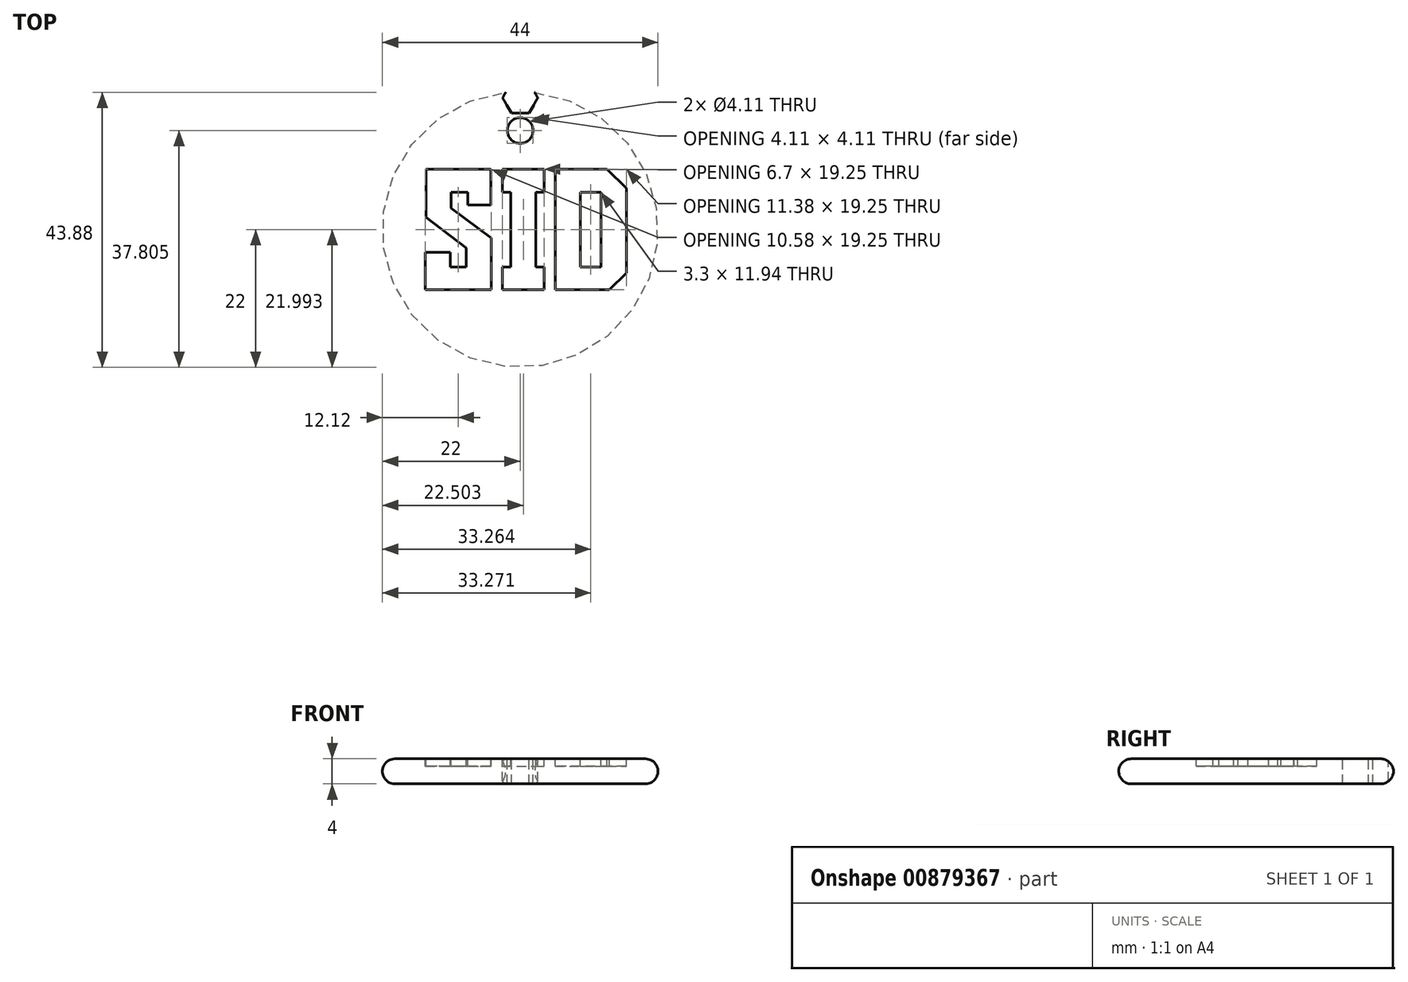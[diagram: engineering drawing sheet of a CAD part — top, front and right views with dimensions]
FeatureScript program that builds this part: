
annotation { "Feature Type Name" : "Feature", "Feature Type Description" : "" }
export const myFeature = defineFeature(function(context is Context, id is Id, definition is map)
    precondition{}
    {
        {
            var Q0;
            Q0=qCreatedBy(makeId("Front.planeOp"),FACE);
            var sketch = newSketch(context, id + "F0", { "sketchPlane" : qUnion([Q0])});
            skLineSegment(sketch, "E0.bottom", {"start": v(0, 0) * mm, "end": v(-20, 0) * mm});
            skLineSegment(sketch, "E0.top", {"start": v(0, 4) * mm, "end": v(-20, 4) * mm});
            skLineSegment(sketch, "E0.left", {"start": v(0, 0) * mm, "end": v(0, 4) * mm});
            skLineSegment(sketch, "E0.right", {"start": v(-20, 0) * mm, "end": v(-20, 4) * mm});
            skArc(sketch, "E1", {"start": v(-20, 4) * mm, "mid": v(-22, 2) * mm, "end": v(-20, 0) * mm});
            skSolve(sketch);
        }
        {
            var Q0;
            Q0=makeQuery(id+"F0.imprint","IMPRINT",FACE,{"disambiguationData":[TD([[makeQuery(id+"F0.imprint","IMPRINT",EDGE,{"derivedFrom":sQuery(id+"F0.wireOp",EDGE,"E0.right")}),1.0]])]});
            var Q1;
            Q1=makeQuery(id+"F0.imprint","IMPRINT",FACE,{"disambiguationData":[TD([[makeQuery(id+"F0.imprint","IMPRINT",EDGE,{"derivedFrom":sQuery(id+"F0.wireOp",EDGE,"E0.bottom")}),-1.0]])]});
            var Q2;
            Q2=sQuery(id+"F0.wireOp",EDGE,"E0.left");
            revolve(context, id + "F1", {"surfaceOperationType" : NewSurfaceOperationType.NEW, "entities" : qUnion([Q0, Q1]), "axis" : qUnion([Q2]), "revolveType" : RevolveType.FULL});
        }
        {
            var Q0;
            Q0=makeQuery(id+"F1.opRevolve","SWEPT_FACE",FACE,{"disambiguationData":[OSD([sQuery(id+"F0.wireOp",EDGE,"E0.top")])]});
            var sketch = newSketch(context, id + "F2", { "sketchPlane" : qUnion([Q0])});
            skLineSegment(sketch, "E2", {"start": v(-4.59, -9.62) * mm, "end": v(-15.17, -9.62) * mm});
            skLineSegment(sketch, "E3", {"start": v(-15.17, -9.62) * mm, "end": v(-15.17, -3.63) * mm});
            skLineSegment(sketch, "E4", {"start": v(-15.17, -3.63) * mm, "end": v(-11.14, -3.63) * mm});
            skLineSegment(sketch, "E5", {"start": v(-11.14, -3.63) * mm, "end": v(-11.14, -5.98) * mm});
            skLineSegment(sketch, "E6", {"start": v(-11.14, -5.98) * mm, "end": v(-8.64, -5.98) * mm});
            skLineSegment(sketch, "E7", {"start": v(-8.64, -5.98) * mm, "end": v(-8.64, -2.92) * mm});
            skLineSegment(sketch, "E8", {"start": v(-8.64, -2.92) * mm, "end": v(-15.04, 1.92) * mm});
            skLineSegment(sketch, "E9", {"start": v(-15.04, 1.92) * mm, "end": v(-15.04, 9.62) * mm});
            skLineSegment(sketch, "E10", {"start": v(-15.04, 9.62) * mm, "end": v(-4.7, 9.62) * mm});
            skLineSegment(sketch, "E11", {"start": v(-4.7, 9.62) * mm, "end": v(-4.7, 3.9) * mm});
            skLineSegment(sketch, "E12", {"start": v(-4.7, 3.9) * mm, "end": v(-8.37, 3.9) * mm});
            skLineSegment(sketch, "E13", {"start": v(-8.37, 3.9) * mm, "end": v(-8.37, 5.95) * mm});
            skLineSegment(sketch, "E14", {"start": v(-8.37, 5.95) * mm, "end": v(-11, 5.95) * mm});
            skLineSegment(sketch, "E15", {"start": v(-11, 5.95) * mm, "end": v(-11, 3.43) * mm});
            skLineSegment(sketch, "E16", {"start": v(-11, 3.43) * mm, "end": v(-4.59, -1.38) * mm});
            skLineSegment(sketch, "E17", {"start": v(-4.59, -1.38) * mm, "end": v(-4.59, -9.62) * mm});
            skLineSegment(sketch, "E18", {"start": v(3.85, -5.98) * mm, "end": v(3.85, -9.62) * mm});
            skLineSegment(sketch, "E19", {"start": v(3.85, -9.62) * mm, "end": v(-2.85, -9.62) * mm});
            skLineSegment(sketch, "E20", {"start": v(-2.85, -9.62) * mm, "end": v(-2.85, -5.98) * mm});
            skLineSegment(sketch, "E21", {"start": v(-2.85, -5.98) * mm, "end": v(-1.51, -5.98) * mm});
            skLineSegment(sketch, "E22", {"start": v(-1.51, -5.98) * mm, "end": v(-1.51, 5.98) * mm});
            skLineSegment(sketch, "E23", {"start": v(-1.51, 5.98) * mm, "end": v(-2.85, 5.98) * mm});
            skLineSegment(sketch, "E24", {"start": v(-2.85, 5.98) * mm, "end": v(-2.85, 9.62) * mm});
            skLineSegment(sketch, "E25", {"start": v(-2.85, 9.62) * mm, "end": v(3.85, 9.62) * mm});
            skLineSegment(sketch, "E26", {"start": v(3.85, 9.62) * mm, "end": v(3.85, 5.98) * mm});
            skLineSegment(sketch, "E27", {"start": v(3.85, 5.98) * mm, "end": v(2.52, 5.98) * mm});
            skLineSegment(sketch, "E28", {"start": v(2.52, 5.98) * mm, "end": v(2.52, -5.98) * mm});
            skLineSegment(sketch, "E29", {"start": v(2.52, -5.98) * mm, "end": v(3.85, -5.98) * mm});
            skLineSegment(sketch, "E30", {"start": v(5.58, 9.62) * mm, "end": v(13.86, 9.62) * mm});
            skLineSegment(sketch, "E31", {"start": v(13.86, 9.62) * mm, "end": v(16.96, 6.58) * mm});
            skLineSegment(sketch, "E32", {"start": v(16.96, 6.58) * mm, "end": v(16.96, -6.96) * mm});
            skLineSegment(sketch, "E33", {"start": v(16.96, -6.96) * mm, "end": v(14.26, -9.62) * mm});
            skLineSegment(sketch, "E34", {"start": v(14.26, -9.62) * mm, "end": v(5.58, -9.62) * mm});
            skLineSegment(sketch, "E35", {"start": v(5.58, -9.62) * mm, "end": v(5.58, 9.62) * mm});
            skLineSegment(sketch, "E36", {"start": v(12.92, -5.98) * mm, "end": v(12.92, 5.96) * mm});
            skLineSegment(sketch, "E37", {"start": v(12.92, 5.96) * mm, "end": v(9.61, 5.96) * mm});
            skLineSegment(sketch, "E38", {"start": v(9.61, 5.96) * mm, "end": v(9.61, -5.98) * mm});
            skLineSegment(sketch, "E39", {"start": v(9.61, -5.98) * mm, "end": v(12.92, -5.98) * mm});
            skSolve(sketch);
        }
        {
            var Q0;
            Q0 = qSketchRegion(id + "F2", true);
            extrude(context, id + "F3", {"entities" : qUnion([Q0]), "operationType" : NewBodyOperationType.REMOVE, "oppositeDirection" : true, "depth" : 1.2 * mm, "offsetDistance" : 25.4 * mm});
        }
        {
            var Q0;
            Q0=makeQuery(id+"F3.boolean.opBoolean","SPLIT",FACE,{"disambiguationData":[TD([makeQuery(id+"F1.opRevolve","SWEPT_FACE",FACE,{"disambiguationData":[OSD([sQuery(id+"F0.wireOp",EDGE,"E1")])]})])],"derivedFrom":makeQuery(id+"F1.opRevolve","SWEPT_FACE",FACE,{"disambiguationData":[OSD([sQuery(id+"F0.wireOp",EDGE,"E0.top")])]})});
            var sketch = newSketch(context, id + "F4", { "sketchPlane" : qUnion([Q0])});
            skCircle(sketch, "E40.cCircle", {"center": v(0, 21.03) * mm, "radius": 2.44 * mm, "construction": true});
            skLineSegment(sketch, "E40.0", {"start": v(1.4, 18.6) * mm, "end": v(-1.4, 18.6) * mm});
            skLineSegment(sketch, "E40.1", {"start": v(-1.4, 18.6) * mm, "end": v(-2.82, 21.03) * mm});
            skLineSegment(sketch, "E40.2", {"start": v(-2.82, 21.03) * mm, "end": v(-1.4, 23.47) * mm});
            skLineSegment(sketch, "E40.3", {"start": v(-1.4, 23.47) * mm, "end": v(1.4, 23.47) * mm});
            skLineSegment(sketch, "E40.4", {"start": v(1.4, 23.47) * mm, "end": v(2.82, 21.03) * mm});
            skLineSegment(sketch, "E40.5", {"start": v(2.82, 21.03) * mm, "end": v(1.4, 18.6) * mm});
            skPoint(sketch, "E40.0.midPoint", {"position": v(0, 18.6) * mm});
            skSolve(sketch);
        }
        {
            var Q0;
            Q0=makeQuery(id+"FIBRFEHrzJW4N2J_1.1.F4.imprint","IMPRINT",FACE,{"disambiguationData":[TD([[makeQuery(id+"FIBRFEHrzJW4N2J_1.1.F4.imprint","IMPRINT",EDGE,{"derivedFrom":sQuery(id+"FIBRFEHrzJW4N2J_1.1.F4.wireOp",EDGE,"E40.0")}),-1.0]])]});
            var Q1;
            Q1=makeQuery(id+"FIBRFEHrzJW4N2J_1.2.F4.imprint","IMPRINT",FACE,{"disambiguationData":[TD([[makeQuery(id+"FIBRFEHrzJW4N2J_1.2.F4.imprint","IMPRINT",EDGE,{"derivedFrom":sQuery(id+"FIBRFEHrzJW4N2J_1.2.F4.wireOp",EDGE,"E40.0")}),-1.0]])]});
            var Q2;
            Q2=makeQuery(id+"FIBRFEHrzJW4N2J_1.3.F4.imprint","IMPRINT",FACE,{"disambiguationData":[TD([[makeQuery(id+"FIBRFEHrzJW4N2J_1.3.F4.imprint","IMPRINT",EDGE,{"derivedFrom":sQuery(id+"FIBRFEHrzJW4N2J_1.3.F4.wireOp",EDGE,"E40.0")}),-1.0]])]});
            var Q3;
            Q3=makeQuery(id+"FIBRFEHrzJW4N2J_1.4.F4.imprint","IMPRINT",FACE,{"disambiguationData":[TD([[makeQuery(id+"FIBRFEHrzJW4N2J_1.4.F4.imprint","IMPRINT",EDGE,{"derivedFrom":sQuery(id+"FIBRFEHrzJW4N2J_1.4.F4.wireOp",EDGE,"E40.0")}),-1.0]])]});
            var Q4;
            Q4=makeQuery(id+"FIBRFEHrzJW4N2J_1.5.F4.imprint","IMPRINT",FACE,{"disambiguationData":[TD([[makeQuery(id+"FIBRFEHrzJW4N2J_1.5.F4.imprint","IMPRINT",EDGE,{"derivedFrom":sQuery(id+"FIBRFEHrzJW4N2J_1.5.F4.wireOp",EDGE,"E40.0")}),-1.0]])]});
            var Q5;
            Q5=makeQuery(id+"FIBRFEHrzJW4N2J_1.6.F4.imprint","IMPRINT",FACE,{"disambiguationData":[TD([[makeQuery(id+"FIBRFEHrzJW4N2J_1.6.F4.imprint","IMPRINT",EDGE,{"derivedFrom":sQuery(id+"FIBRFEHrzJW4N2J_1.6.F4.wireOp",EDGE,"E40.0")}),-1.0]])]});
            var Q6;
            Q6=makeQuery(id+"FIBRFEHrzJW4N2J_1.7.F4.imprint","IMPRINT",FACE,{"disambiguationData":[TD([[makeQuery(id+"FIBRFEHrzJW4N2J_1.7.F4.imprint","IMPRINT",EDGE,{"derivedFrom":sQuery(id+"FIBRFEHrzJW4N2J_1.7.F4.wireOp",EDGE,"E40.0")}),-1.0]])]});
            var Q7;
            Q7=makeQuery(id+"FIBRFEHrzJW4N2J_1.8.F4.imprint","IMPRINT",FACE,{"disambiguationData":[TD([[makeQuery(id+"FIBRFEHrzJW4N2J_1.8.F4.imprint","IMPRINT",EDGE,{"derivedFrom":sQuery(id+"FIBRFEHrzJW4N2J_1.8.F4.wireOp",EDGE,"E40.0")}),-1.0]])]});
            var Q8;
            Q8=makeQuery(id+"FIBRFEHrzJW4N2J_1.9.F4.imprint","IMPRINT",FACE,{"disambiguationData":[TD([[makeQuery(id+"FIBRFEHrzJW4N2J_1.9.F4.imprint","IMPRINT",EDGE,{"derivedFrom":sQuery(id+"FIBRFEHrzJW4N2J_1.9.F4.wireOp",EDGE,"E40.0")}),-1.0]])]});
            var Q9;
            Q9=makeQuery(id+"FIBRFEHrzJW4N2J_1.10.F4.imprint","IMPRINT",FACE,{"disambiguationData":[TD([[makeQuery(id+"FIBRFEHrzJW4N2J_1.10.F4.imprint","IMPRINT",EDGE,{"derivedFrom":sQuery(id+"FIBRFEHrzJW4N2J_1.10.F4.wireOp",EDGE,"E40.0")}),-1.0]])]});
            var Q10;
            Q10=makeQuery(id+"FIBRFEHrzJW4N2J_1.11.F4.imprint","IMPRINT",FACE,{"disambiguationData":[TD([[makeQuery(id+"FIBRFEHrzJW4N2J_1.11.F4.imprint","IMPRINT",EDGE,{"derivedFrom":sQuery(id+"FIBRFEHrzJW4N2J_1.11.F4.wireOp",EDGE,"E40.0")}),-1.0]])]});
            var Q11;
            {var subQ6=sQuery(id+"F4.wireOp",EDGE,"E40.2");Q11=makeQuery(id+"F4.imprint","IMPRINT",FACE,{"disambiguationData":[TD([[makeQuery(id+"F4.imprint","IMPRINT",EDGE,{"derivedFrom":subQ6}),-1.0]])]});}
            var Q12;
            {var subQ0=sQuery(id+"F4.wireOp",EDGE,"E40.0");Q12=makeQuery(id+"F4.imprint","IMPRINT",FACE,{"disambiguationData":[TD([[makeQuery(id+"F4.imprint","IMPRINT",EDGE,{"derivedFrom":subQ0}),-1.0]])]});}
            extrude(context, id + "F5", {"entities" : qUnion([Q0, Q1, Q2, Q3, Q4, Q5, Q6, Q7, Q8, Q9, Q10, Q11, Q12]), "operationType" : NewBodyOperationType.REMOVE, "oppositeDirection" : true, "depth" : 25.4 * mm, "offsetDistance" : 25.4 * mm});
        }
        {
            var Q0;
            Q0=makeQuery(id+"F3.boolean.opBoolean","SPLIT",FACE,{"disambiguationData":[TD([makeQuery(id+"F1.opRevolve","SWEPT_FACE",FACE,{"disambiguationData":[OSD([sQuery(id+"F0.wireOp",EDGE,"E1")])]})])],"derivedFrom":makeQuery(id+"F1.opRevolve","SWEPT_FACE",FACE,{"disambiguationData":[OSD([sQuery(id+"F0.wireOp",EDGE,"E0.top")])]})});
            var sketch = newSketch(context, id + "F6", { "sketchPlane" : qUnion([Q0])});
            skCircle(sketch, "E41", {"center": v(0, 15.8) * mm, "radius": 2.05 * mm});
            skSolve(sketch);
        }
        {
            var Q0;
            Q0 = qSketchRegion(id + "F6", true);
            extrude(context, id + "F7", {"entities" : qUnion([Q0]), "operationType" : NewBodyOperationType.REMOVE, "oppositeDirection" : true, "depth" : 25.4 * mm, "offsetDistance" : 25.4 * mm});
        }
    });
